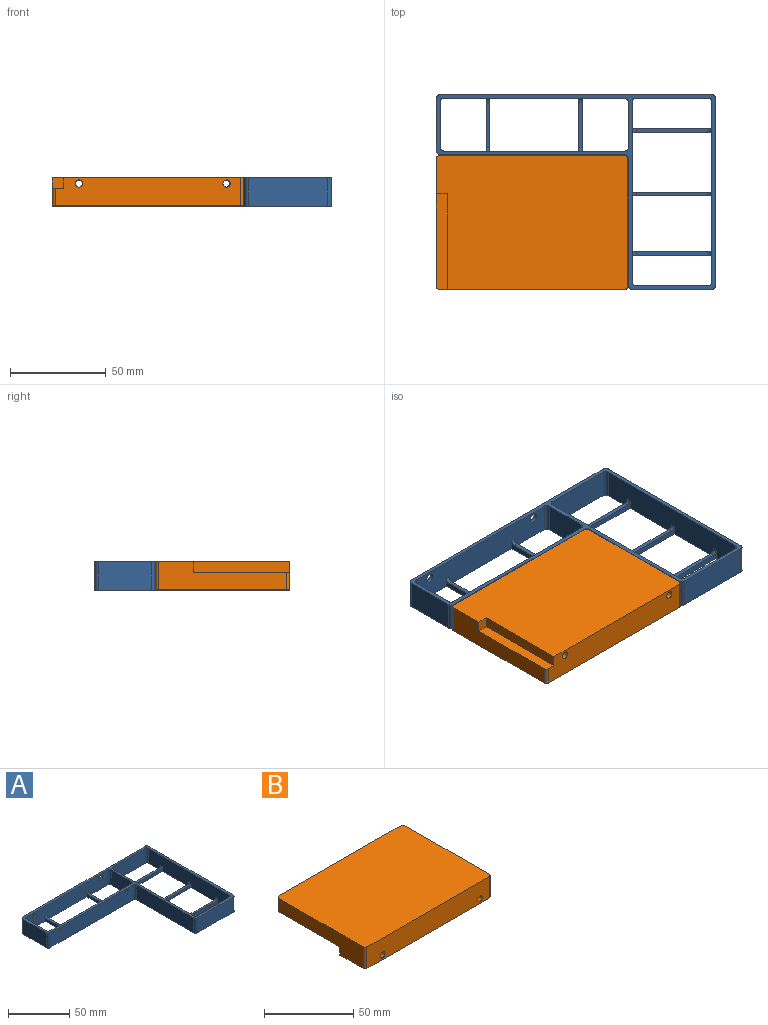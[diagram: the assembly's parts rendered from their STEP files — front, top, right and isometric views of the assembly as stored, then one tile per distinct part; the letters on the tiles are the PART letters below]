
ASSEMBLY  parts=2 mates=1
PART A: 59 faces, bbox 146x102x15 mm
  f0: plane 94x15mm, normal (1,0,0), area 1380mm2, adj f14,f15,f26,f27,f29,f30,f32,f33
  f1: plane 94.4x15mm, normal (0,-1,0), area 1356.7mm2, adj f14,f15,f16,f17,f20,f21,f23,f24
  f2: plane 37.6x15mm, normal (0,1,0), area 564mm2, adj f14,f15,f52,f58
  f3: plane 37.6x15mm, normal (0,-1,0), area 564mm2, adj f14,f15,f56,f57
  f4: plane 94.4x15mm, normal (0,1,0), area 1373.3mm2, adj f14,f15,f18,f19,f20,f21,f23,f24
  f5: plane 23.6x15mm, normal (1,0,0), area 354mm2, adj f14,f15,f47,f49
  f6: plane 27.6x15mm, normal (-1,0,0), area 414mm2, adj f14,f15,f48,f51
  f7: plane 96.4x15mm, normal (0,-1,0), area 1423.3mm2, adj f14,f15,f18,f19,f45,f48
  f8: plane 66.4x15mm, normal (-1,0,0), area 996mm2, adj f14,f15,f45,f53
  f9: plane 41.6x15mm, normal (0,-1,0), area 624mm2, adj f14,f15,f53,f54
  f10: plane 98x15mm, normal (1,0,0), area 1470mm2, adj f14,f15,f54,f55
  f11: plane 23.6x15mm, normal (-1,0,0), area 354mm2, adj f14,f15,f46,f50
  f12: plane 142x15mm, normal (0,1,0), area 2090.7mm2, adj f14,f15,f16,f17,f51,f55
  f13: plane 94x15mm, normal (-1,0,0), area 1380mm2, adj f14,f15,f26,f27,f29,f30,f32,f33
  f14: plane 146x102mm, normal (0,0,1), area 1034.6mm2, adj f0,f1,f2,f3,f4,f5,f6,f7
  f15: plane 146x102mm, normal (0,0,-1), area 1394.6mm2, adj f0,f1,f2,f3,f4,f5,f6,f7
  f16: cylinder r=2.5mm len=5mm, axis (0,1,0), area 31.4mm2, adj f1,f12
  f17: cylinder r=2.5mm len=5mm, axis (0,1,0), area 31.4mm2, adj f1,f12
  f18: cylinder r=1.9mm len=3.8mm, axis (0,1,0), area 23.9mm2, adj f4,f7
  f19: cylinder r=1.9mm len=3.8mm, axis (0,1,0), area 23.9mm2, adj f4,f7
  f20: plane 27.6x5mm, normal (-1,0,0), area 84.5mm2, adj f1,f4,f15,f22,f43,f44
  f21: plane 27.6x5mm, normal (1,0,0), area 84.5mm2, adj f1,f4,f15,f22,f43,f44
  f22: plane 23.6x2mm, normal (0,0,1), area 47.2mm2, adj f20,f21,f43,f44
  f23: plane 27.6x5mm, normal (-1,0,0), area 84.5mm2, adj f1,f4,f15,f25,f41,f42
  f24: plane 27.6x5mm, normal (1,0,0), area 84.5mm2, adj f1,f4,f15,f25,f41,f42
  f25: plane 23.6x2mm, normal (0,0,1), area 47.2mm2, adj f23,f24,f41,f42
  f26: plane 41.6x5mm, normal (0,1,0), area 126.5mm2, adj f0,f13,f15,f28,f39,f40
  f27: plane 41.6x5mm, normal (0,-1,0), area 126.5mm2, adj f0,f13,f15,f28,f39,f40
  f28: plane 37.6x2mm, normal (0,0,1), area 75.2mm2, adj f26,f27,f39,f40
  f29: plane 41.6x5mm, normal (0,-1,0), area 126.5mm2, adj f0,f13,f15,f31,f37,f38
  f30: plane 41.6x5mm, normal (0,1,0), area 126.5mm2, adj f0,f13,f15,f31,f37,f38
  f31: plane 37.6x2mm, normal (0,0,1), area 75.2mm2, adj f29,f30,f37,f38
  f32: plane 41.6x5mm, normal (0,1,0), area 126.5mm2, adj f0,f13,f15,f34,f35,f36
  f33: plane 41.6x5mm, normal (0,-1,0), area 126.5mm2, adj f0,f13,f15,f34,f35,f36
  f34: plane 37.6x2mm, normal (0,0,1), area 75.2mm2, adj f32,f33,f35,f36
  f35: cylinder r=2mm len=2mm, axis (0,1,0), area 6.3mm2, adj f0,f32,f33,f34
  f36: cylinder r=2mm len=2mm, axis (0,-1,0), area 6.3mm2, adj f13,f32,f33,f34
  f37: cylinder r=2mm len=2mm, axis (0,-1,0), area 6.3mm2, adj f13,f29,f30,f31
  f38: cylinder r=2mm len=2mm, axis (0,1,0), area 6.3mm2, adj f0,f29,f30,f31
  f39: cylinder r=2mm len=2mm, axis (0,1,0), area 6.3mm2, adj f0,f26,f27,f28
  f40: cylinder r=2mm len=2mm, axis (0,-1,0), area 6.3mm2, adj f13,f26,f27,f28
  f41: cylinder r=2mm len=2mm, axis (-1,0,0), area 6.3mm2, adj f4,f23,f24,f25
  f42: cylinder r=2mm len=2mm, axis (1,0,0), area 6.3mm2, adj f1,f23,f24,f25
  f43: cylinder r=2mm len=2mm, axis (-1,0,0), area 6.3mm2, adj f4,f20,f21,f22
  f44: cylinder r=2mm len=2mm, axis (1,0,0), area 6.3mm2, adj f1,f20,f21,f22
  f45: cylinder r=2mm len=15mm, axis (0,0,-1), area 47.1mm2, adj f7,f8,f14,f15
  f46: cylinder r=2mm len=15mm, axis (0,0,1), area 47.1mm2, adj f4,f11,f14,f15
  f47: cylinder r=2mm len=15mm, axis (0,0,1), area 47.1mm2, adj f4,f5,f14,f15
  f48: cylinder r=2mm len=15mm, axis (0,0,-1), area 47.1mm2, adj f6,f7,f14,f15
  f49: cylinder r=2mm len=15mm, axis (0,0,-1), area 47.1mm2, adj f1,f5,f14,f15
  f50: cylinder r=2mm len=15mm, axis (0,0,-1), area 47.1mm2, adj f1,f11,f14,f15
  f51: cylinder r=2mm len=15mm, axis (0,0,1), area 47.1mm2, adj f6,f12,f14,f15
  f52: cylinder r=2mm len=15mm, axis (0,0,-1), area 47.1mm2, adj f0,f2,f14,f15
  f53: cylinder r=2mm len=15mm, axis (0,0,1), area 47.1mm2, adj f8,f9,f14,f15
  f54: cylinder r=2mm len=15mm, axis (0,0,-1), area 47.1mm2, adj f9,f10,f14,f15
  f55: cylinder r=2mm len=15mm, axis (0,0,1), area 47.1mm2, adj f10,f12,f14,f15
  f56: cylinder r=2mm len=15mm, axis (0,0,1), area 47.1mm2, adj f0,f3,f14,f15
  f57: cylinder r=2mm len=15mm, axis (0,0,-1), area 47.1mm2, adj f3,f13,f14,f15
  f58: cylinder r=2mm len=15mm, axis (0,0,1), area 47.1mm2, adj f2,f13,f14,f15
PART B: 15 faces, bbox 100x70x14.8 mm
  f0: plane 100x70mm, normal (0,0,-1), area 6713.6mm2, adj f1,f2,f3,f4,f6,f7,f11,f12
  f1: plane 97x14.8mm, normal (0,1,0), area 1389mm2, adj f0,f5,f7,f8,f9,f10,f12,f13
  f2: plane 67x14.8mm, normal (-1,0,0), area 715.2mm2, adj f0,f5,f6,f8,f13,f14
  f3: plane 97x14.8mm, normal (0,-1,0), area 1412.9mm2, adj f0,f5,f9,f10,f11,f14
  f4: plane 67x14.8mm, normal (1,0,0), area 991.6mm2, adj f0,f5,f11,f12
  f5: plane 100x70mm, normal (0,0,1), area 6998.1mm2, adj f1,f2,f3,f4,f11,f12,f13,f14
  f6: plane 5.7x5.7mm, normal (0,1,0), area 32.5mm2, adj f0,f2,f7,f8
  f7: plane 50x5.7mm, normal (-1,0,0), area 285mm2, adj f0,f1,f6,f8
  f8: plane 50x5.7mm, normal (0,0,-1), area 284.5mm2, adj f1,f2,f6,f7,f13
  f9: cylinder r=1.9mm len=70mm, axis (0,-1,0), area 835.7mm2, adj f1,f3
  f10: cylinder r=1.9mm len=70mm, axis (0,-1,0), area 835.7mm2, adj f1,f3
  f11: cylinder r=1.5mm len=14.8mm, axis (0,0,1), area 34.9mm2, adj f0,f3,f4,f5
  f12: cylinder r=1.5mm len=14.8mm, axis (0,0,-1), area 34.9mm2, adj f0,f1,f4,f5
  f13: cylinder r=1.5mm len=9.1mm, axis (0,0,1), area 21.4mm2, adj f1,f2,f5,f8
  f14: cylinder r=1.5mm len=14.8mm, axis (0,0,-1), area 34.9mm2, adj f0,f2,f3,f5
PLACE A t=(-11.98,8.33,14.37)mm
PLACE B rot(axis=(1,0,0),180deg) t=(-34.98,-7.67,29.37)mm
MATE fastened B.f10 <-> A.f18  axis (0,1,0) through (-71.08,27.33,26.27)mm
